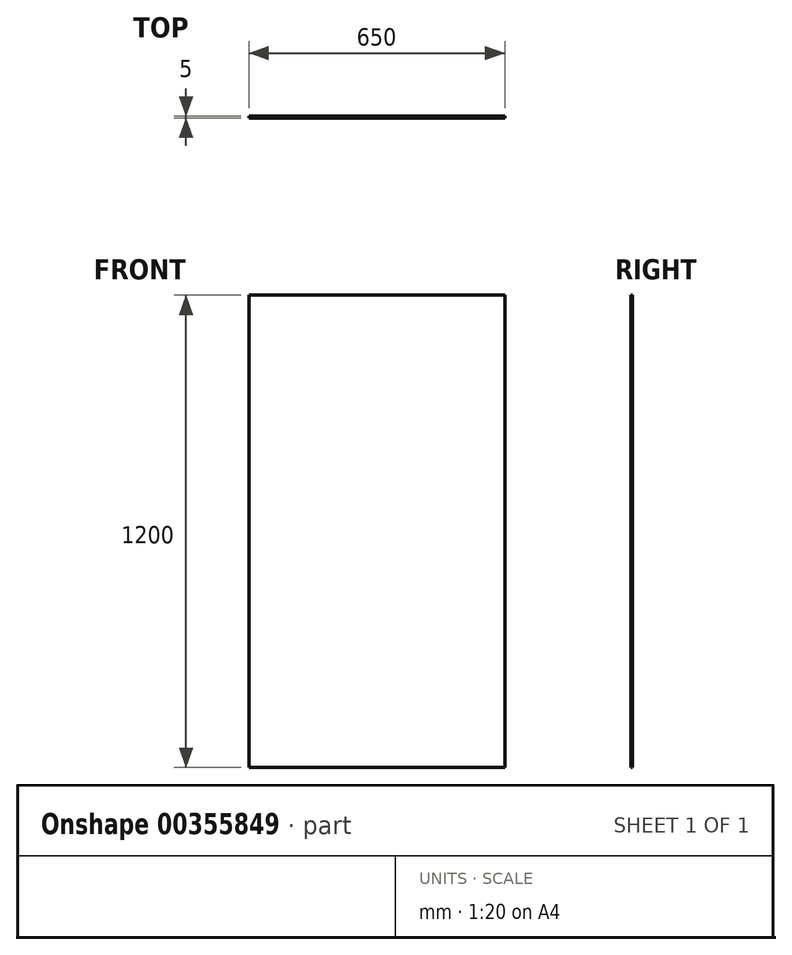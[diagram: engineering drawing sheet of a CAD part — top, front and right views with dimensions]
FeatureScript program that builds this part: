
annotation { "Feature Type Name" : "Feature", "Feature Type Description" : "" }
export const myFeature = defineFeature(function(context is Context, id is Id, definition is map)
    precondition{}
    {
        {
            var Q0;
            Q0=qCreatedBy(makeId("Front.planeOp"),FACE);
            var sketch = newSketch(context, id + "F0", { "sketchPlane" : qUnion([Q0])});
            skLineSegment(sketch, "E0.bottom", {"start": v(-12.05, 1076.62) * mm, "end": v(637.95, 1076.62) * mm});
            skLineSegment(sketch, "E0.top", {"start": v(-12.05, -123.38) * mm, "end": v(637.95, -123.38) * mm});
            skLineSegment(sketch, "E0.left", {"start": v(-12.05, 1076.62) * mm, "end": v(-12.05, -123.38) * mm});
            skLineSegment(sketch, "E0.right", {"start": v(637.95, 1076.62) * mm, "end": v(637.95, -123.38) * mm});
            skSolve(sketch);
        }
        {
            var Q0;
            Q0 = qSketchRegion(id + "F0", true);
            extrude(context, id + "F1", {"entities" : qUnion([Q0]), "depth" : 5 * mm});
        }
    });
